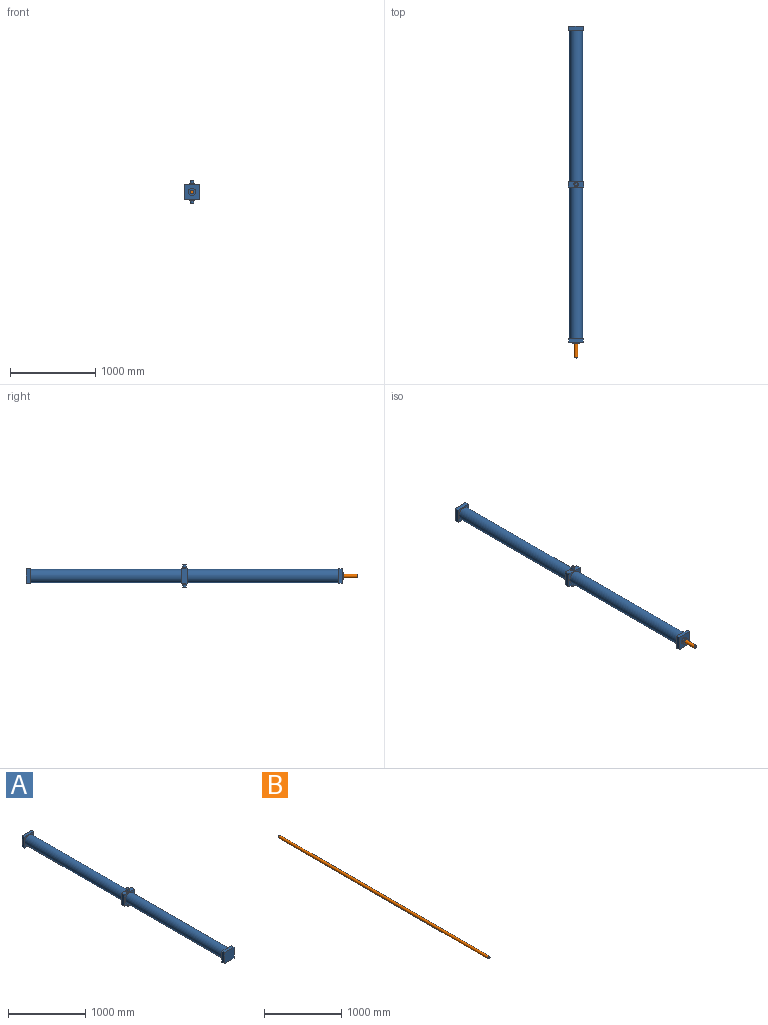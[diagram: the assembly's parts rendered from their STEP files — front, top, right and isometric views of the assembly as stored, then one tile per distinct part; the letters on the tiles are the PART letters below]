
ASSEMBLY  parts=2 mates=1
PART A: 34 faces, bbox 185x3728x264 mm
  f0: plane 174x48mm, normal (-1,0,0), area 8352mm2, adj f1,f3,f4,f5
  f1: plane 174x48mm, normal (0,0,-1), area 8352mm2, adj f0,f2,f4,f5
  f2: plane 174x48mm, normal (1,0,0), area 8352mm2, adj f1,f3,f4,f5
  f3: plane 174x48mm, normal (0,0,1), area 8352mm2, adj f0,f2,f4,f5
  f4: plane 174x174mm, normal (0,1,0), area 11649.5mm2, adj f0,f1,f2,f3,f6
  f5: plane 174x174mm, normal (0,-1,0), area 30276mm2, adj f0,f1,f2,f3
  f6: cylinder r=77mm len=1780mm, axis (0,-1,0), area 861173.4mm2, adj f4,f12
  f7: plane 185x60mm, normal (1,0,0), area 11100mm2, adj f8,f10,f11,f12
  f8: plane 185x60mm, normal (0,0,-1), area 9136.5mm2, adj f7,f9,f11,f12,f24
  f9: plane 185x60mm, normal (-1,0,0), area 11100mm2, adj f8,f10,f11,f12
  f10: plane 185x60mm, normal (0,0,1), area 9136.5mm2, adj f7,f9,f11,f12,f29
  f11: plane 185x185mm, normal (0,1,0), area 15598.5mm2, adj f7,f8,f9,f10,f13
  f12: plane 185x185mm, normal (0,-1,0), area 15598.5mm2, adj f6,f7,f8,f9,f10
  f13: cylinder r=77mm len=1780mm, axis (0,-1,0), area 861173.4mm2, adj f11,f19
  f14: plane 174x40mm, normal (1,0,0), area 6960mm2, adj f15,f17,f18,f19
  f15: plane 174x40mm, normal (0,0,-1), area 6960mm2, adj f14,f16,f18,f19
  f16: plane 174x40mm, normal (-1,0,0), area 6960mm2, adj f15,f17,f18,f19
  f17: plane 174x40mm, normal (0,0,1), area 6960mm2, adj f14,f16,f18,f19
  f18: plane 174x174mm, normal (0,1,0), area 24601.5mm2, adj f14,f15,f16,f17,f20
  f19: plane 174x174mm, normal (0,-1,0), area 11649.5mm2, adj f13,f14,f15,f16,f17
  f20: cylinder r=42.5mm len=85mm, axis (0,-1,0), area 5340.7mm2, adj f18,f21
  f21: plane 85x85mm, normal (0,1,0), area 4417.9mm2, adj f20,f22
  f22: cylinder r=20mm len=3680mm, axis (0,1,0), area 462442.4mm2, adj f21,f23
  f23: plane 40x40mm, normal (0,1,0), area 1256.6mm2, adj f22
  f24: cylinder r=25mm len=50mm, axis (0,0,1), area 706.9mm2, adj f8,f25
  f25: plane 50x50mm, normal (0,0,-1), area 301.6mm2, adj f24,f28
  f26: plane 40x40mm, normal (0,0,-1), area 1256.6mm2, adj f27
  f27: cylinder r=20mm len=40mm, axis (0,0,1), area 4021.2mm2, adj f26,f28
  f28: torus R=23mm, axis (0,0,-1), area 624.5mm2, adj f25,f27
  f29: cylinder r=25mm len=50mm, axis (0,0,-1), area 706.9mm2, adj f10,f30
  f30: plane 50x50mm, normal (0,0,1), area 301.6mm2, adj f29,f33
  f31: plane 40x40mm, normal (0,0,1), area 1256.6mm2, adj f32
  f32: cylinder r=20mm len=40mm, axis (0,0,-1), area 4021.2mm2, adj f31,f33
  f33: torus R=23mm, axis (0,0,1), area 624.5mm2, adj f30,f32
PART B: 4 faces, bbox 40x3845x40 mm
  f0: cylinder r=20mm len=3843mm, axis (0,-1,0), area 482925.6mm2, adj f1,f3
  f1: plane 40x40mm, normal (0,1,0), area 1256.6mm2, adj f0
  f2: plane 36x36mm, normal (0,-1,0), area 1017.9mm2, adj f3
  f3: cone r=18mm half-angle=45deg, axis (0,1,0), area 337.7mm2, adj f0,f2
PLACE A rot(axis=(0,0,1),180deg) t=(0,3708,0)mm
PLACE B t=(-87,-185,87)mm
MATE slider B.f0 <-> A.f6  axis (0,1,0) through (-87,3660,87)mm
